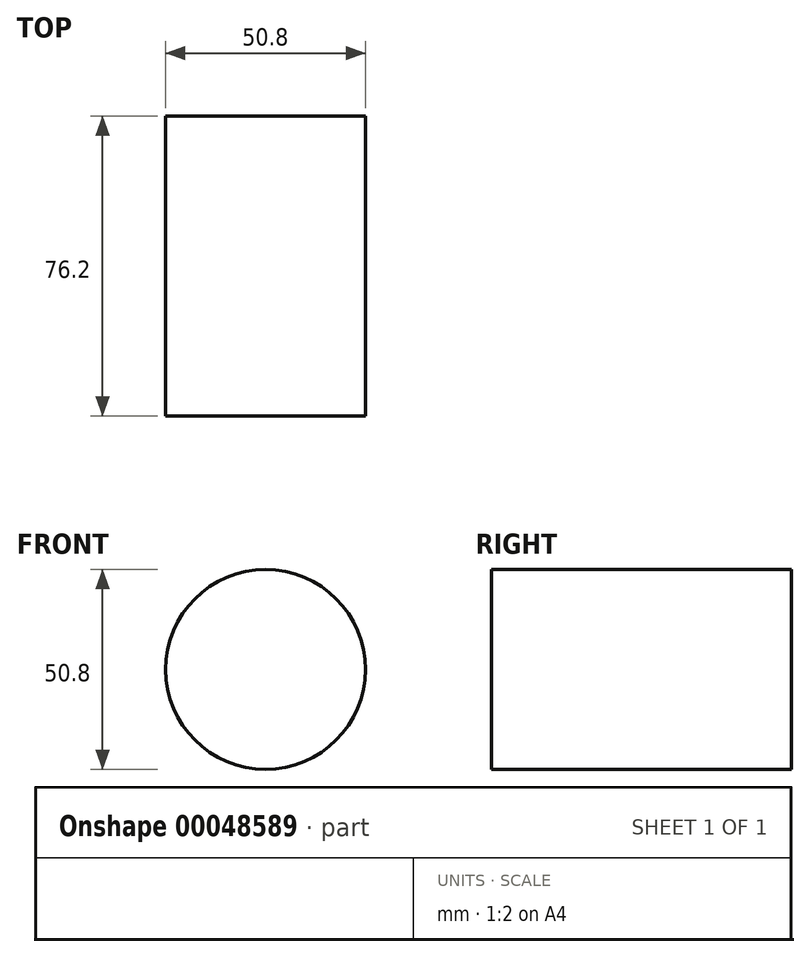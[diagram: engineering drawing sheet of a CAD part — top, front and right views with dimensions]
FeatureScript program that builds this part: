
annotation { "Feature Type Name" : "Feature", "Feature Type Description" : "" }
export const myFeature = defineFeature(function(context is Context, id is Id, definition is map)
    precondition{}
    {
        {
            var Q0;
            Q0=qCreatedBy(makeId("Front.planeOp"),FACE);
            var sketch = newSketch(context, id + "F0", { "sketchPlane" : qUnion([Q0])});
            skCircle(sketch, "E0", {"center": v(0, 0) * mm, "radius": 25.4 * mm});
            skCircle(sketch, "E1", {"center": v(-76.2, 0) * mm, "radius": 12.7 * mm});
            skLineSegment(sketch, "E2", {"start": v(-78.32, 12.52) * mm, "end": v(-4.23, 25.04) * mm});
            skLineSegment(sketch, "E3", {"start": v(-78.32, -12.52) * mm, "end": v(-4.23, -25.04) * mm});
            skSolve(sketch);
        }
        {
            var Q0;
            {var subQ0=sQuery(id+"F0.wireOp",EDGE,"E0");var subQ2=makeQuery(id+"F0.imprint","INTERSECT",VERTEX,{"derivedFrom":[subQ0,sQuery(id+"F0.wireOp",EDGE,"E2")]});Q0=makeQuery(id+"F0.imprint","IMPRINT",FACE,{"disambiguationData":[TD([[makeQuery(id+"F0.imprint","IMPRINT",EDGE,{"disambiguationData":[TD([[subQ2,-1.0]])],"derivedFrom":subQ0}),1.0]])]});}
            extrude(context, id + "F1", {"entities" : qUnion([Q0]), "depth" : 76.2 * mm});
        }
    });
